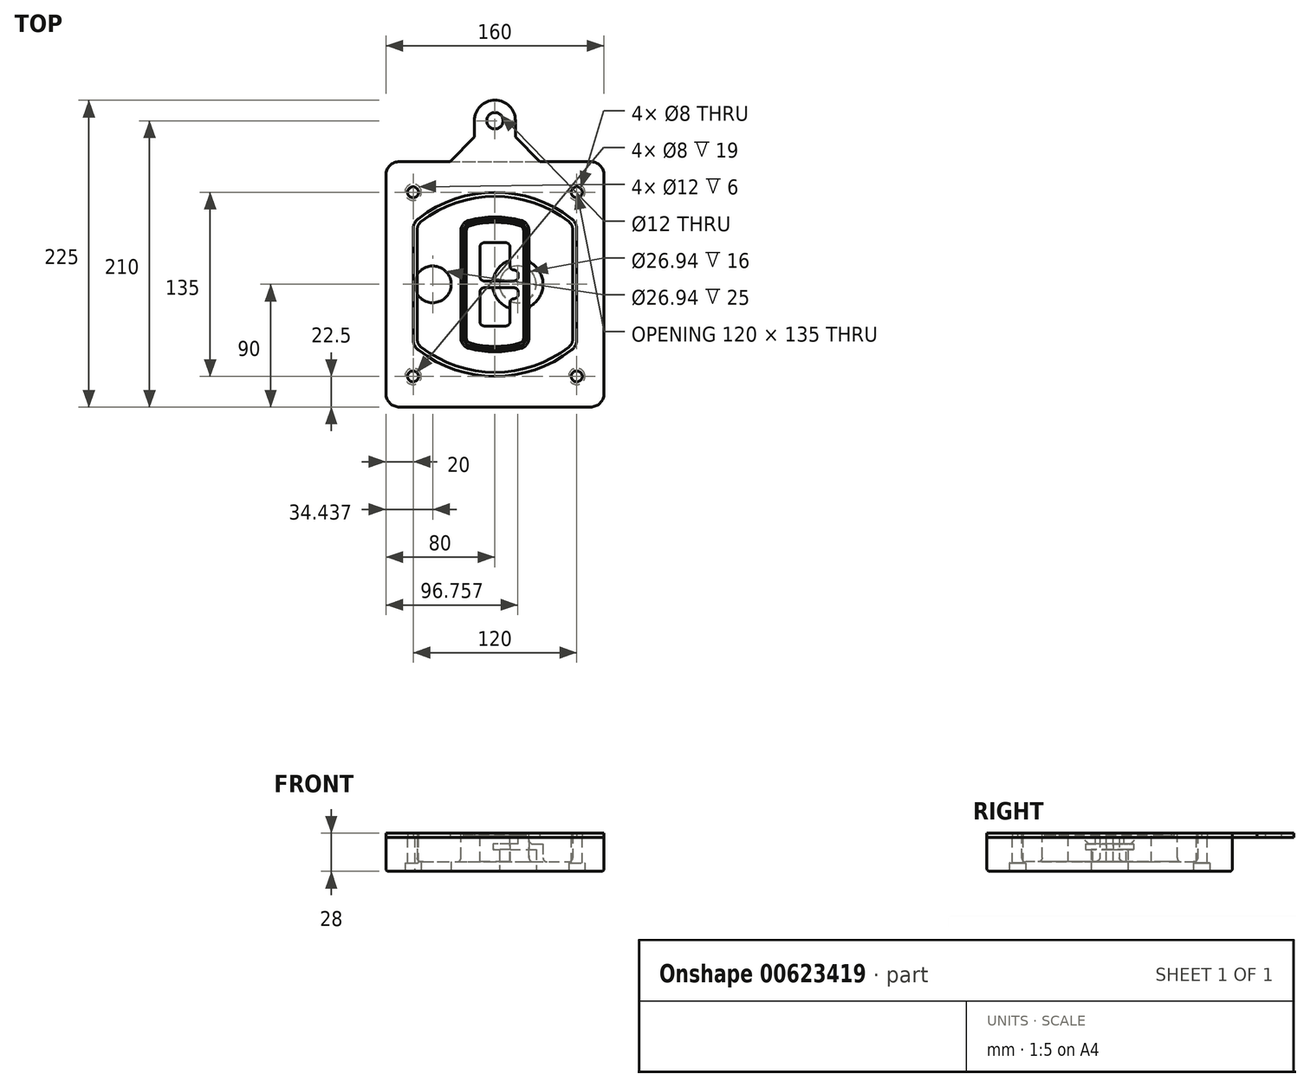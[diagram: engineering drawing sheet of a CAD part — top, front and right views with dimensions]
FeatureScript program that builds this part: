
annotation { "Feature Type Name" : "Feature", "Feature Type Description" : "" }
export const myFeature = defineFeature(function(context is Context, id is Id, definition is map)
    precondition{}
    {
        {
            var Q0;
            Q0=qCreatedBy(makeId("Top.planeOp"),FACE);
            var sketch = newSketch(context, id + "F0", { "sketchPlane" : qUnion([Q0])});
            skPoint(sketch, "E0.rect.middle", {"position": v(0, 0) * mm});
            skLineSegment(sketch, "E1.bottom", {"start": v(-70, -90) * mm, "end": v(70, -90) * mm});
            skLineSegment(sketch, "E1.top", {"start": v(-70, 90) * mm, "end": v(70, 90) * mm});
            skLineSegment(sketch, "E1.left", {"start": v(-80, -80) * mm, "end": v(-80, 80) * mm});
            skLineSegment(sketch, "E1.right", {"start": v(80, -80) * mm, "end": v(80, 80) * mm});
            skLineSegment(sketch, "E2", {"start": v(-80, 90) * mm, "end": v(80, -90) * mm, "construction": true});
            skLineSegment(sketch, "E3", {"start": v(80, 90) * mm, "end": v(-80, -90) * mm, "construction": true});
            skCircle(sketch, "E4", {"center": v(-60, 67.5) * mm, "radius": 4 * mm});
            skCircle(sketch, "E5", {"center": v(60, 67.5) * mm, "radius": 4 * mm});
            skCircle(sketch, "E6", {"center": v(60, -67.5) * mm, "radius": 4 * mm});
            skCircle(sketch, "E7", {"center": v(-60, -67.5) * mm, "radius": 4 * mm});
            skLineSegment(sketch, "E8", {"start": v(-60, 67.5) * mm, "end": v(60, 67.5) * mm, "construction": true});
            skLineSegment(sketch, "E9", {"start": v(60, 67.5) * mm, "end": v(60, -67.5) * mm, "construction": true});
            skLineSegment(sketch, "E10", {"start": v(60, -67.5) * mm, "end": v(-60, -67.5) * mm, "construction": true});
            skLineSegment(sketch, "E11", {"start": v(-60, -67.5) * mm, "end": v(-60, 67.5) * mm, "construction": true});
            skLineSegment(sketch, "E12", {"start": v(-60, 40.3) * mm, "end": v(-60, -40.3) * mm});
            skLineSegment(sketch, "E13", {"start": v(60, 40.3) * mm, "end": v(60, -40.3) * mm});
            skArc(sketch, "E14", {"start": v(56.15, 48.18) * mm, "mid": v(0, 67.5) * mm, "end": v(-56.15, 48.18) * mm});
            skArc(sketch, "E15", {"start": v(-56.15, -48.18) * mm, "mid": v(0, -67.5) * mm, "end": v(56.15, -48.18) * mm});
            skLineSegment(sketch, "E16", {"start": v(-60, 0) * mm, "end": v(60, 0) * mm, "construction": true});
            skPoint(sketch, "E17.visualSharp", {"position": v(-60, -45) * mm});
            skArc(sketch, "E17.filletArc", {"start": v(-60, -40.3) * mm, "mid": v(-58.99, -44.68) * mm, "end": v(-56.15, -48.18) * mm});
            skPoint(sketch, "E18.visualSharp", {"position": v(-60, 45) * mm});
            skArc(sketch, "E18.filletArc", {"start": v(-56.15, 48.18) * mm, "mid": v(-58.99, 44.68) * mm, "end": v(-60, 40.3) * mm});
            skPoint(sketch, "E19.visualSharp", {"position": v(60, 45) * mm});
            skArc(sketch, "E19.filletArc", {"start": v(60, 40.3) * mm, "mid": v(58.99, 44.68) * mm, "end": v(56.15, 48.18) * mm});
            skPoint(sketch, "E20.visualSharp", {"position": v(60, -45) * mm});
            skArc(sketch, "E20.filletArc", {"start": v(56.15, -48.18) * mm, "mid": v(58.99, -44.68) * mm, "end": v(60, -40.3) * mm});
            skPoint(sketch, "E21.visualSharp", {"position": v(-80, 90) * mm});
            skArc(sketch, "E21.filletArc", {"start": v(-70, 90) * mm, "mid": v(-77.07, 87.07) * mm, "end": v(-80, 80) * mm});
            skPoint(sketch, "E22.visualSharp", {"position": v(80, 90) * mm});
            skArc(sketch, "E22.filletArc", {"start": v(80, 80) * mm, "mid": v(77.07, 87.07) * mm, "end": v(70, 90) * mm});
            skPoint(sketch, "E23.visualSharp", {"position": v(80, -90) * mm});
            skArc(sketch, "E23.filletArc", {"start": v(70, -90) * mm, "mid": v(77.07, -87.07) * mm, "end": v(80, -80) * mm});
            skPoint(sketch, "E24.visualSharp", {"position": v(-80, -90) * mm});
            skArc(sketch, "E24.filletArc", {"start": v(-80, -80) * mm, "mid": v(-77.07, -87.07) * mm, "end": v(-70, -90) * mm});
            skArc(sketch, "E25.0", {"start": v(57, 40.3) * mm, "mid": v(56.3, 43.36) * mm, "end": v(54.3, 45.81) * mm});
            skLineSegment(sketch, "E25.1", {"start": v(57, 40.3) * mm, "end": v(57, -40.3) * mm});
            skArc(sketch, "E25.2", {"start": v(54.3, -45.81) * mm, "mid": v(56.3, -43.36) * mm, "end": v(57, -40.3) * mm});
            skArc(sketch, "E25.3", {"start": v(-54.3, -45.81) * mm, "mid": v(0, -64.5) * mm, "end": v(54.3, -45.81) * mm});
            skArc(sketch, "E25.4", {"start": v(-57, -40.3) * mm, "mid": v(-56.3, -43.36) * mm, "end": v(-54.3, -45.81) * mm});
            skArc(sketch, "E25.5", {"start": v(54.3, 45.81) * mm, "mid": v(0, 64.5) * mm, "end": v(-54.3, 45.81) * mm});
            skLineSegment(sketch, "E25.6", {"start": v(-57, 40.3) * mm, "end": v(-57, -40.3) * mm});
            skArc(sketch, "E25.7", {"start": v(-54.3, 45.81) * mm, "mid": v(-56.3, 43.36) * mm, "end": v(-57, 40.3) * mm});
            skArc(sketch, "E26.0", {"start": v(-58.62, 51.33) * mm, "mid": v(-62.58, 46.43) * mm, "end": v(-64, 40.3) * mm});
            skArc(sketch, "E26.1", {"start": v(58.62, 51.33) * mm, "mid": v(0, 71.5) * mm, "end": v(-58.62, 51.33) * mm});
            skArc(sketch, "E26.2", {"start": v(64, 40.3) * mm, "mid": v(62.58, 46.43) * mm, "end": v(58.62, 51.33) * mm});
            skLineSegment(sketch, "E26.3", {"start": v(64, 40.3) * mm, "end": v(64, -40.3) * mm});
            skArc(sketch, "E26.4", {"start": v(58.62, -51.33) * mm, "mid": v(62.58, -46.43) * mm, "end": v(64, -40.3) * mm});
            skLineSegment(sketch, "E26.5", {"start": v(-64, 40.3) * mm, "end": v(-64, -40.3) * mm});
            skArc(sketch, "E26.6", {"start": v(-58.62, -51.33) * mm, "mid": v(0, -71.5) * mm, "end": v(58.62, -51.33) * mm});
            skArc(sketch, "E26.7", {"start": v(-64, -40.3) * mm, "mid": v(-62.58, -46.43) * mm, "end": v(-58.62, -51.33) * mm});
            skSolve(sketch);
        }
        {
            var Q0;
            Q0=makeQuery(id+"F0.imprint","IMPRINT",FACE,{"disambiguationData":[TD([[makeQuery(id+"F0.imprint","IMPRINT",EDGE,{"derivedFrom":sQuery(id+"F0.wireOp",EDGE,"E1.bottom")}),1.0]])]});
            var Q1;
            Q1=makeQuery(id+"F0.imprint","IMPRINT",FACE,{"disambiguationData":[TD([[makeQuery(id+"F0.imprint","IMPRINT",EDGE,{"derivedFrom":sQuery(id+"F0.wireOp",EDGE,"E12")}),1.0]])]});
            var Q2;
            Q2=makeQuery(id+"F0.imprint","IMPRINT",FACE,{"disambiguationData":[TD([[makeQuery(id+"F0.imprint","IMPRINT",EDGE,{"derivedFrom":sQuery(id+"F0.wireOp",EDGE,"E25.0")}),1.0]])]});
            var Q3;
            Q3=makeQuery(id+"F0.imprint","IMPRINT",FACE,{"disambiguationData":[TD([[makeQuery(id+"F0.imprint","IMPRINT",EDGE,{"derivedFrom":sQuery(id+"F0.wireOp",EDGE,"E12")}),-1.0]])]});
            extrude(context, id + "F1", {"entities" : qUnion([Q0, Q1, Q2, Q3]), "oppositeDirection" : true, "depth" : 25 * mm});
        }
        {
            var Q0;
            Q0=makeQuery(id+"F0.imprint","IMPRINT",FACE,{"disambiguationData":[TD([[makeQuery(id+"F0.imprint","IMPRINT",EDGE,{"derivedFrom":sQuery(id+"F0.wireOp",EDGE,"E12")}),1.0]])]});
            extrude(context, id + "F2", {"entities" : qUnion([Q0]), "operationType" : NewBodyOperationType.ADD, "depth" : 3 * mm});
        }
        {
            var Q0;
            Q0=makeQuery(id+"F0.imprint","IMPRINT",FACE,{"disambiguationData":[TD([[makeQuery(id+"F0.imprint","IMPRINT",EDGE,{"derivedFrom":sQuery(id+"F0.wireOp",EDGE,"E25.0")}),1.0]])]});
            extrude(context, id + "F3", {"entities" : qUnion([Q0]), "operationType" : NewBodyOperationType.REMOVE, "oppositeDirection" : true, "depth" : 18 * mm});
        }
        {
            var Q0;
            Q0=makeQuery(id+"F2.opExtrude","CAP_FACE",FACE,{"disambiguationData":[OSD([sQuery(id+"F0.wireOp",EDGE,"E12"),sQuery(id+"F0.wireOp",EDGE,"E13"),sQuery(id+"F0.wireOp",EDGE,"E14"),sQuery(id+"F0.wireOp",EDGE,"E15"),sQuery(id+"F0.wireOp",EDGE,"E17.filletArc"),sQuery(id+"F0.wireOp",EDGE,"E18.filletArc"),sQuery(id+"F0.wireOp",EDGE,"E19.filletArc"),sQuery(id+"F0.wireOp",EDGE,"E20.filletArc"),sQuery(id+"F0.wireOp",EDGE,"E25.0"),sQuery(id+"F0.wireOp",EDGE,"E25.1"),sQuery(id+"F0.wireOp",EDGE,"E25.2"),sQuery(id+"F0.wireOp",EDGE,"E25.3"),sQuery(id+"F0.wireOp",EDGE,"E25.4"),sQuery(id+"F0.wireOp",EDGE,"E25.5"),sQuery(id+"F0.wireOp",EDGE,"E25.6"),sQuery(id+"F0.wireOp",EDGE,"E25.7")])],"isStart":false});
            var sketch = newSketch(context, id + "F4", { "sketchPlane" : qUnion([Q0])});
            skArc(sketch, "E27.0", {"start": v(-19.08, -46.97) * mm, "mid": v(0, -49.5) * mm, "end": v(19.08, -46.97) * mm});
            skArc(sketch, "E28.0", {"start": v(19.08, 46.97) * mm, "mid": v(0, 49.5) * mm, "end": v(-19.08, 46.97) * mm});
            skLineSegment(sketch, "E29", {"start": v(-25, 39.25) * mm, "end": v(-25, -39.25) * mm});
            skLineSegment(sketch, "E30", {"start": v(25, 39.25) * mm, "end": v(25, -39.25) * mm});
            skLineSegment(sketch, "E31", {"start": v(-25, 45.1) * mm, "end": v(25, 45.1) * mm, "construction": true});
            skLineSegment(sketch, "E32", {"start": v(-25, -45.1) * mm, "end": v(25, -45.1) * mm, "construction": true});
            skPoint(sketch, "E33.visualSharp", {"position": v(-25, 45.1) * mm});
            skArc(sketch, "E33.filletArc", {"start": v(-19.08, 46.97) * mm, "mid": v(-23.35, 44.11) * mm, "end": v(-25, 39.25) * mm});
            skPoint(sketch, "E34.visualSharp", {"position": v(25, 45.1) * mm});
            skArc(sketch, "E34.filletArc", {"start": v(25, 39.25) * mm, "mid": v(23.35, 44.11) * mm, "end": v(19.08, 46.97) * mm});
            skPoint(sketch, "E35.visualSharp", {"position": v(25, -45.1) * mm});
            skArc(sketch, "E35.filletArc", {"start": v(19.08, -46.97) * mm, "mid": v(23.35, -44.11) * mm, "end": v(25, -39.25) * mm});
            skPoint(sketch, "E36.visualSharp", {"position": v(-25, -45.1) * mm});
            skArc(sketch, "E36.filletArc", {"start": v(-25, -39.25) * mm, "mid": v(-23.35, -44.11) * mm, "end": v(-19.08, -46.97) * mm});
            skArc(sketch, "E37.0", {"start": v(54.3, 45.81) * mm, "mid": v(0, 64.5) * mm, "end": v(-54.3, 45.81) * mm});
            skArc(sketch, "E37.1", {"start": v(-54.3, 45.81) * mm, "mid": v(-56.3, 43.36) * mm, "end": v(-57, 40.3) * mm});
            skLineSegment(sketch, "E37.2", {"start": v(-57, 40.3) * mm, "end": v(-57, -40.3) * mm});
            skArc(sketch, "E37.3", {"start": v(-57, -40.3) * mm, "mid": v(-56.3, -43.36) * mm, "end": v(-54.3, -45.81) * mm});
            skArc(sketch, "E37.4", {"start": v(-54.3, -45.81) * mm, "mid": v(0, -64.5) * mm, "end": v(54.3, -45.81) * mm});
            skArc(sketch, "E37.5", {"start": v(54.3, -45.81) * mm, "mid": v(56.3, -43.36) * mm, "end": v(57, -40.3) * mm});
            skLineSegment(sketch, "E37.6", {"start": v(57, 40.3) * mm, "end": v(57, -40.3) * mm});
            skArc(sketch, "E37.7", {"start": v(57, 40.3) * mm, "mid": v(56.3, 43.36) * mm, "end": v(54.3, 45.81) * mm});
            skLineSegment(sketch, "E38.0", {"start": v(23, 39.25) * mm, "end": v(23, -39.25) * mm});
            skArc(sketch, "E38.1", {"start": v(18.56, -45.04) * mm, "mid": v(21.76, -42.9) * mm, "end": v(23, -39.25) * mm});
            skArc(sketch, "E38.2", {"start": v(-18.56, -45.04) * mm, "mid": v(0, -47.5) * mm, "end": v(18.56, -45.04) * mm});
            skArc(sketch, "E38.3", {"start": v(-23, -39.25) * mm, "mid": v(-21.76, -42.9) * mm, "end": v(-18.56, -45.04) * mm});
            skLineSegment(sketch, "E38.4", {"start": v(-23, 39.25) * mm, "end": v(-23, -39.25) * mm});
            skArc(sketch, "E38.5", {"start": v(23, 39.25) * mm, "mid": v(21.76, 42.9) * mm, "end": v(18.56, 45.04) * mm});
            skArc(sketch, "E38.6", {"start": v(-18.56, 45.04) * mm, "mid": v(-21.76, 42.9) * mm, "end": v(-23, 39.25) * mm});
            skArc(sketch, "E38.7", {"start": v(18.56, 45.04) * mm, "mid": v(0, 47.5) * mm, "end": v(-18.56, 45.04) * mm});
            skArc(sketch, "E39.0", {"start": v(21, 39.25) * mm, "mid": v(20.18, 41.68) * mm, "end": v(18.04, 43.1) * mm});
            skLineSegment(sketch, "E39.1", {"start": v(21, 39.25) * mm, "end": v(21, -39.25) * mm});
            skArc(sketch, "E39.2", {"start": v(18.04, -43.1) * mm, "mid": v(20.18, -41.68) * mm, "end": v(21, -39.25) * mm});
            skArc(sketch, "E39.3", {"start": v(-18.04, -43.1) * mm, "mid": v(0, -45.5) * mm, "end": v(18.04, -43.1) * mm});
            skArc(sketch, "E39.4", {"start": v(-21, -39.25) * mm, "mid": v(-20.18, -41.68) * mm, "end": v(-18.04, -43.1) * mm});
            skArc(sketch, "E39.5", {"start": v(18.04, 43.1) * mm, "mid": v(0, 45.5) * mm, "end": v(-18.04, 43.1) * mm});
            skLineSegment(sketch, "E39.6", {"start": v(-21, 39.25) * mm, "end": v(-21, -39.25) * mm});
            skArc(sketch, "E39.7", {"start": v(-18.04, 43.1) * mm, "mid": v(-20.18, 41.68) * mm, "end": v(-21, 39.25) * mm});
            skLineSegment(sketch, "E40", {"start": v(-25, 0) * mm, "end": v(25, 0) * mm, "construction": true});
            skLineSegment(sketch, "E41", {"start": v(-11, 5.5) * mm, "end": v(-11, 27.5) * mm});
            skLineSegment(sketch, "E42", {"start": v(-8, 30.5) * mm, "end": v(8, 30.5) * mm});
            skLineSegment(sketch, "E43", {"start": v(11, 27.5) * mm, "end": v(11, 13.5) * mm});
            skLineSegment(sketch, "E44", {"start": v(14, 10.5) * mm, "end": v(14, 10.5) * mm});
            skLineSegment(sketch, "E45", {"start": v(17, 7.5) * mm, "end": v(17, 5.5) * mm});
            skLineSegment(sketch, "E46", {"start": v(14, 2.5) * mm, "end": v(-8, 2.5) * mm});
            skPoint(sketch, "E47.visualSharp", {"position": v(-11, 30.5) * mm});
            skArc(sketch, "E47.filletArc", {"start": v(-8, 30.5) * mm, "mid": v(-10.12, 29.62) * mm, "end": v(-11, 27.5) * mm});
            skPoint(sketch, "E48.visualSharp", {"position": v(11, 30.5) * mm});
            skArc(sketch, "E48.filletArc", {"start": v(11, 27.5) * mm, "mid": v(10.12, 29.62) * mm, "end": v(8, 30.5) * mm});
            skPoint(sketch, "E49.visualSharp", {"position": v(11, 10.5) * mm});
            skArc(sketch, "E49.filletArc", {"start": v(11, 13.5) * mm, "mid": v(11.88, 11.38) * mm, "end": v(14, 10.5) * mm});
            skPoint(sketch, "E50.visualSharp", {"position": v(17, 10.5) * mm});
            skArc(sketch, "E50.filletArc", {"start": v(17, 7.5) * mm, "mid": v(16.12, 9.62) * mm, "end": v(14, 10.5) * mm});
            skPoint(sketch, "E51.visualSharp", {"position": v(17, 2.5) * mm});
            skArc(sketch, "E51.filletArc", {"start": v(14, 2.5) * mm, "mid": v(16.12, 3.38) * mm, "end": v(17, 5.5) * mm});
            skPoint(sketch, "E52.visualSharp", {"position": v(-11, 2.5) * mm});
            skArc(sketch, "E52.filletArc", {"start": v(-11, 5.5) * mm, "mid": v(-10.12, 3.38) * mm, "end": v(-8, 2.5) * mm});
            skLineSegment(sketch, "E53.0.MirrorCS", {"start": v(14, -2.5) * mm, "end": v(-8, -2.5) * mm});
            skArc(sketch, "E54.0.MirrorCS", {"start": v(-11, -5.5) * mm, "mid": v(-10.12, -3.38) * mm, "end": v(-8, -2.5) * mm});
            skLineSegment(sketch, "E55.0.MirrorCS", {"start": v(-11, -5.5) * mm, "end": v(-11, -27.5) * mm});
            skArc(sketch, "E56.0.MirrorCS", {"start": v(-8, -30.5) * mm, "mid": v(-10.12, -29.62) * mm, "end": v(-11, -27.5) * mm});
            skLineSegment(sketch, "E57.0.MirrorCS", {"start": v(-8, -30.5) * mm, "end": v(8, -30.5) * mm});
            skArc(sketch, "E58.0.MirrorCS", {"start": v(11, -27.5) * mm, "mid": v(10.12, -29.62) * mm, "end": v(8, -30.5) * mm});
            skLineSegment(sketch, "E59.0.MirrorCS", {"start": v(11, -27.5) * mm, "end": v(11, -13.5) * mm});
            skArc(sketch, "E60.0.MirrorCS", {"start": v(11, -13.5) * mm, "mid": v(11.88, -11.38) * mm, "end": v(14, -10.5) * mm});
            skArc(sketch, "E61.0.MirrorCS", {"start": v(17, -7.5) * mm, "mid": v(16.12, -9.62) * mm, "end": v(14, -10.5) * mm});
            skLineSegment(sketch, "E62.0.MirrorCS", {"start": v(17, -7.5) * mm, "end": v(17, -5.5) * mm});
            skArc(sketch, "E63.0.MirrorCS", {"start": v(14, -2.5) * mm, "mid": v(16.12, -3.38) * mm, "end": v(17, -5.5) * mm});
            skSolve(sketch);
        }
        {
            var Q0;
            Q0=makeQuery(id+"F4.imprint","IMPRINT",FACE,{"disambiguationData":[TD([[makeQuery(id+"F4.imprint","IMPRINT",EDGE,{"derivedFrom":sQuery(id+"F4.wireOp",EDGE,"E27.0")}),1.0]])]});
            var Q1;
            Q1=makeQuery(id+"F4.imprint","IMPRINT",FACE,{"disambiguationData":[TD([[makeQuery(id+"F4.imprint","IMPRINT",EDGE,{"derivedFrom":sQuery(id+"F4.wireOp",EDGE,"E38.0")}),-1.0]])]});
            var Q2;
            Q2=makeQuery(id+"F4.imprint","IMPRINT",FACE,{"disambiguationData":[TD([[makeQuery(id+"F4.imprint","IMPRINT",EDGE,{"derivedFrom":sQuery(id+"F4.wireOp",EDGE,"E39.0")}),1.0]])]});
            extrude(context, id + "F5", {"entities" : qUnion([Q0, Q1, Q2]), "operationType" : NewBodyOperationType.ADD, "endBound" : BoundingType.UP_TO_NEXT, "oppositeDirection" : true, "depth" : 25 * mm});
        }
        {
            var Q0;
            Q0=makeQuery(id+"F4.imprint","IMPRINT",FACE,{"disambiguationData":[TD([[makeQuery(id+"F4.imprint","IMPRINT",EDGE,{"derivedFrom":sQuery(id+"F4.wireOp",EDGE,"E38.0")}),-1.0]])]});
            extrude(context, id + "F6", {"entities" : qUnion([Q0]), "operationType" : NewBodyOperationType.REMOVE, "oppositeDirection" : true, "depth" : 2 * mm});
        }
        {
            var Q0;
            Q0=makeQuery(id+"F1.opExtrude","CAP_FACE",FACE,{"disambiguationData":[OSD([sQuery(id+"F0.wireOp",EDGE,"E1.bottom"),sQuery(id+"F0.wireOp",EDGE,"E1.top"),sQuery(id+"F0.wireOp",EDGE,"E1.left"),sQuery(id+"F0.wireOp",EDGE,"E1.right"),sQuery(id+"F0.wireOp",EDGE,"E4"),sQuery(id+"F0.wireOp",EDGE,"E5"),sQuery(id+"F0.wireOp",EDGE,"E6"),sQuery(id+"F0.wireOp",EDGE,"E7"),sQuery(id+"F0.wireOp",EDGE,"E21.filletArc"),sQuery(id+"F0.wireOp",EDGE,"E22.filletArc"),sQuery(id+"F0.wireOp",EDGE,"E23.filletArc"),sQuery(id+"F0.wireOp",EDGE,"E24.filletArc")])],"isStart":false});
            var sketch = newSketch(context, id + "F7", { "sketchPlane" : qUnion([Q0])});
            skCircle(sketch, "E64", {"center": v(16.76, 0) * mm, "radius": 13.47 * mm});
            skCircle(sketch, "E65", {"center": v(-45.56, 0) * mm, "radius": 13.47 * mm});
            skLineSegment(sketch, "E66", {"start": v(80, 0) * mm, "end": v(-80, 0) * mm});
            skCircle(sketch, "E67", {"center": v(16.76, 0) * mm, "radius": 18.47 * mm});
            skCircle(sketch, "E68", {"center": v(60, -67.5) * mm, "radius": 6 * mm});
            skCircle(sketch, "E69", {"center": v(-60, -67.5) * mm, "radius": 6 * mm});
            skCircle(sketch, "E70", {"center": v(-60, 67.5) * mm, "radius": 6 * mm});
            skCircle(sketch, "E71", {"center": v(60, 67.5) * mm, "radius": 6 * mm});
            skSolve(sketch);
        }
        {
            var Q0;
            {var subQ1=sQuery(id+"F7.wireOp",EDGE,"E66");var subQ4=sQuery(id+"F7.wireOp",EDGE,"E64");var subQ6=makeQuery(id+"F7.imprint","INTERSECT",VERTEX,{"disambiguationData":[OD(0.0)],"derivedFrom":[subQ4,subQ1]});Q0=makeQuery(id+"F7.imprint","IMPRINT",FACE,{"disambiguationData":[TD([[makeQuery(id+"F7.imprint","IMPRINT",EDGE,{"disambiguationData":[TD([[subQ6,-1.0]])],"derivedFrom":subQ4}),-1.0]])]});}
            var Q1;
            {var subQ0=sQuery(id+"F7.wireOp",EDGE,"E66");var subQ1=sQuery(id+"F7.wireOp",EDGE,"E64");var subQ3=makeQuery(id+"F7.imprint","INTERSECT",VERTEX,{"disambiguationData":[OD(0.0)],"derivedFrom":[subQ1,subQ0]});Q1=makeQuery(id+"F7.imprint","IMPRINT",FACE,{"disambiguationData":[TD([[makeQuery(id+"F7.imprint","IMPRINT",EDGE,{"disambiguationData":[TD([[subQ3,-1.0]])],"derivedFrom":subQ1}),1.0]])]});}
            var Q2;
            {var subQ0=sQuery(id+"F7.wireOp",EDGE,"E66");var subQ1=sQuery(id+"F7.wireOp",EDGE,"E64");var subQ3=makeQuery(id+"F7.imprint","INTERSECT",VERTEX,{"disambiguationData":[OD(0.0)],"derivedFrom":[subQ1,subQ0]});Q2=makeQuery(id+"F7.imprint","IMPRINT",FACE,{"disambiguationData":[TD([[makeQuery(id+"F7.imprint","IMPRINT",EDGE,{"disambiguationData":[TD([[subQ3,1.0]])],"derivedFrom":subQ1}),1.0]])]});}
            var Q3;
            {var subQ1=sQuery(id+"F7.wireOp",EDGE,"E66");var subQ4=sQuery(id+"F7.wireOp",EDGE,"E64");var subQ6=makeQuery(id+"F7.imprint","INTERSECT",VERTEX,{"disambiguationData":[OD(0.0)],"derivedFrom":[subQ4,subQ1]});Q3=makeQuery(id+"F7.imprint","IMPRINT",FACE,{"disambiguationData":[TD([[makeQuery(id+"F7.imprint","IMPRINT",EDGE,{"disambiguationData":[TD([[subQ6,1.0]])],"derivedFrom":subQ4}),-1.0]])]});}
            extrude(context, id + "F8", {"entities" : qUnion([Q0, Q1, Q2, Q3]), "operationType" : NewBodyOperationType.ADD, "oppositeDirection" : true, "depth" : 20 * mm});
        }
        {
            var Q0;
            {var subQ0=sQuery(id+"F7.wireOp",EDGE,"E66");var subQ1=sQuery(id+"F7.wireOp",EDGE,"E64");var subQ3=makeQuery(id+"F7.imprint","INTERSECT",VERTEX,{"disambiguationData":[OD(0.0)],"derivedFrom":[subQ1,subQ0]});Q0=makeQuery(id+"F7.imprint","IMPRINT",FACE,{"disambiguationData":[TD([[makeQuery(id+"F7.imprint","IMPRINT",EDGE,{"disambiguationData":[TD([[subQ3,-1.0]])],"derivedFrom":subQ1}),1.0]])]});}
            var Q1;
            {var subQ0=sQuery(id+"F7.wireOp",EDGE,"E66");var subQ1=sQuery(id+"F7.wireOp",EDGE,"E64");var subQ3=makeQuery(id+"F7.imprint","INTERSECT",VERTEX,{"disambiguationData":[OD(0.0)],"derivedFrom":[subQ1,subQ0]});Q1=makeQuery(id+"F7.imprint","IMPRINT",FACE,{"disambiguationData":[TD([[makeQuery(id+"F7.imprint","IMPRINT",EDGE,{"disambiguationData":[TD([[subQ3,1.0]])],"derivedFrom":subQ1}),1.0]])]});}
            extrude(context, id + "F9", {"entities" : qUnion([Q0, Q1]), "operationType" : NewBodyOperationType.REMOVE, "oppositeDirection" : true, "depth" : 16 * mm});
        }
        {
            var Q0;
            {var subQ0=sQuery(id+"F7.wireOp",EDGE,"E66");var subQ1=sQuery(id+"F7.wireOp",EDGE,"E65");var subQ3=makeQuery(id+"F7.imprint","INTERSECT",VERTEX,{"disambiguationData":[OD(0.0)],"derivedFrom":[subQ1,subQ0]});Q0=makeQuery(id+"F7.imprint","IMPRINT",FACE,{"disambiguationData":[TD([[makeQuery(id+"F7.imprint","IMPRINT",EDGE,{"disambiguationData":[TD([[subQ3,-1.0]])],"derivedFrom":subQ1}),1.0]])]});}
            var Q1;
            {var subQ0=sQuery(id+"F7.wireOp",EDGE,"E66");var subQ1=sQuery(id+"F7.wireOp",EDGE,"E65");var subQ3=makeQuery(id+"F7.imprint","INTERSECT",VERTEX,{"disambiguationData":[OD(0.0)],"derivedFrom":[subQ1,subQ0]});Q1=makeQuery(id+"F7.imprint","IMPRINT",FACE,{"disambiguationData":[TD([[makeQuery(id+"F7.imprint","IMPRINT",EDGE,{"disambiguationData":[TD([[subQ3,1.0]])],"derivedFrom":subQ1}),1.0]])]});}
            extrude(context, id + "F10", {"entities" : qUnion([Q0, Q1]), "operationType" : NewBodyOperationType.REMOVE, "oppositeDirection" : true, "depth" : 25 * mm});
        }
        {
            var Q0;
            Q0=makeQuery(id+"F7.imprint","IMPRINT",FACE,{"disambiguationData":[TD([[makeQuery(id+"F7.imprint","IMPRINT",EDGE,{"derivedFrom":sQuery(id+"F7.wireOp",EDGE,"E68")}),1.0]])]});
            var Q1;
            Q1=makeQuery(id+"F7.imprint","IMPRINT",FACE,{"disambiguationData":[TD([[makeQuery(id+"F7.imprint","IMPRINT",EDGE,{"derivedFrom":makeQuery(id+"F1.opExtrude","CAP_EDGE",EDGE,{"disambiguationData":[OSD([sQuery(id+"F0.wireOp",EDGE,"E5")])],"isStart":false})}),-1.0]])]});
            var Q2;
            Q2=makeQuery(id+"F7.imprint","IMPRINT",FACE,{"disambiguationData":[TD([[makeQuery(id+"F7.imprint","IMPRINT",EDGE,{"derivedFrom":sQuery(id+"F7.wireOp",EDGE,"E69")}),1.0]])]});
            var Q3;
            Q3=makeQuery(id+"F7.imprint","IMPRINT",FACE,{"disambiguationData":[TD([[makeQuery(id+"F7.imprint","IMPRINT",EDGE,{"derivedFrom":makeQuery(id+"F1.opExtrude","CAP_EDGE",EDGE,{"disambiguationData":[OSD([sQuery(id+"F0.wireOp",EDGE,"E4")])],"isStart":false})}),-1.0]])]});
            var Q4;
            Q4=makeQuery(id+"F7.imprint","IMPRINT",FACE,{"disambiguationData":[TD([[makeQuery(id+"F7.imprint","IMPRINT",EDGE,{"derivedFrom":sQuery(id+"F7.wireOp",EDGE,"E70")}),1.0]])]});
            var Q5;
            Q5=makeQuery(id+"F7.imprint","IMPRINT",FACE,{"disambiguationData":[TD([[makeQuery(id+"F7.imprint","IMPRINT",EDGE,{"derivedFrom":makeQuery(id+"F1.opExtrude","CAP_EDGE",EDGE,{"disambiguationData":[OSD([sQuery(id+"F0.wireOp",EDGE,"E7")])],"isStart":false})}),-1.0]])]});
            var Q6;
            Q6=makeQuery(id+"F7.imprint","IMPRINT",FACE,{"disambiguationData":[TD([[makeQuery(id+"F7.imprint","IMPRINT",EDGE,{"derivedFrom":sQuery(id+"F7.wireOp",EDGE,"E71")}),1.0]])]});
            var Q7;
            Q7=makeQuery(id+"F7.imprint","IMPRINT",FACE,{"disambiguationData":[TD([[makeQuery(id+"F7.imprint","IMPRINT",EDGE,{"derivedFrom":makeQuery(id+"F1.opExtrude","CAP_EDGE",EDGE,{"disambiguationData":[OSD([sQuery(id+"F0.wireOp",EDGE,"E6")])],"isStart":false})}),-1.0]])]});
            extrude(context, id + "F11", {"entities" : qUnion([Q0, Q1, Q2, Q3, Q4, Q5, Q6, Q7]), "operationType" : NewBodyOperationType.REMOVE, "oppositeDirection" : true, "depth" : 6 * mm});
        }
        {
            var Q0;
            Q0=makeQuery(id+"F9.boolean.opBoolean","COPY",FACE,{"derivedFrom":makeQuery(id+"F9.opExtrude","CAP_FACE",FACE,{"disambiguationData":[OSD([sQuery(id+"F7.wireOp",EDGE,"E64")])],"isStart":false})});
            var sketch = newSketch(context, id + "F12", { "sketchPlane" : qUnion([Q0])});
            skArc(sketch, "E72.0", {"start": v(11, 17.55) * mm, "mid": v(2.57, 11.82) * mm, "end": v(-1.54, 2.5) * mm});
            skArc(sketch, "E72.1", {"start": v(-1.54, -2.5) * mm, "mid": v(2.57, -11.82) * mm, "end": v(11, -17.55) * mm});
            skLineSegment(sketch, "E73", {"start": v(-1.54, -2.5) * mm, "end": v(14, -2.5) * mm});
            skLineSegment(sketch, "E74.0", {"start": v(14, 2.5) * mm, "end": v(-1.54, 2.5) * mm});
            skArc(sketch, "E74.1", {"start": v(14, 2.5) * mm, "mid": v(16.12, 3.38) * mm, "end": v(17, 5.5) * mm});
            skLineSegment(sketch, "E74.2", {"start": v(17, 7.5) * mm, "end": v(17, 5.5) * mm});
            skArc(sketch, "E74.3", {"start": v(17, 7.5) * mm, "mid": v(16.12, 9.62) * mm, "end": v(14, 10.5) * mm});
            skArc(sketch, "E74.4", {"start": v(11, 13.5) * mm, "mid": v(11.88, 11.38) * mm, "end": v(14, 10.5) * mm});
            skLineSegment(sketch, "E74.5", {"start": v(11, 17.55) * mm, "end": v(11, 13.5) * mm});
            skLineSegment(sketch, "E74.7", {"start": v(14, -2.5) * mm, "end": v(-1.54, -2.5) * mm});
            skArc(sketch, "E74.8", {"start": v(14, -2.5) * mm, "mid": v(16.12, -3.38) * mm, "end": v(17, -5.5) * mm});
            skLineSegment(sketch, "E74.9", {"start": v(17, -7.5) * mm, "end": v(17, -5.5) * mm});
            skArc(sketch, "E74.10", {"start": v(17, -7.5) * mm, "mid": v(16.12, -9.62) * mm, "end": v(14, -10.5) * mm});
            skArc(sketch, "E74.11", {"start": v(11, -13.5) * mm, "mid": v(11.88, -11.38) * mm, "end": v(14, -10.5) * mm});
            skLineSegment(sketch, "E74.12", {"start": v(11, -17.55) * mm, "end": v(11, -13.5) * mm});
            skPoint(sketch, "E75.orphan", {"position": v(11, -27.5) * mm});
            skPoint(sketch, "E76.orphan", {"position": v(-8, -2.5) * mm});
            skPoint(sketch, "E77.orphan", {"position": v(-8, 2.5) * mm});
            skPoint(sketch, "E78.orphan", {"position": v(11, 27.5) * mm});
            skSolve(sketch);
        }
        {
            var Q0;
            {var subQ7=sQuery(id+"F12.wireOp",EDGE,"E72.0");var subQ14=sQuery(id+"F12.wireOp",EDGE,"E72.1");var subQ16=sQuery(id+"F12.wireOp",EDGE,"E74.1");var subQ18=sQuery(id+"F12.wireOp",EDGE,"E74.8");Q0=qUnion([makeQuery(id+"F12.imprint","IMPRINT",FACE,{"disambiguationData":[TD([[makeQuery(id+"F12.imprint","IMPRINT",EDGE,{"derivedFrom":subQ7}),1.0]])]}),makeQuery(id+"F12.imprint","IMPRINT",FACE,{"disambiguationData":[TD([[makeQuery(id+"F12.imprint","IMPRINT",EDGE,{"derivedFrom":subQ14}),1.0]])]}),makeQuery(id+"F12.imprint","IMPRINT",FACE,{"disambiguationData":[TD([[makeQuery(id+"F12.imprint","IMPRINT",EDGE,{"derivedFrom":subQ16}),1.0]])]}),makeQuery(id+"F12.imprint","IMPRINT",FACE,{"disambiguationData":[TD([[makeQuery(id+"F12.imprint","IMPRINT",EDGE,{"derivedFrom":subQ18}),-1.0]])]})]);}
            var Q1;
            Q1=makeQuery(id+"F5.boolean.opBoolean","SPLIT",FACE,{"disambiguationData":[TD([makeQuery(id+"F5.opExtrude","SWEPT_FACE",FACE,{"disambiguationData":[OSD([sQuery(id+"F4.wireOp",EDGE,"E41")])]})])],"derivedFrom":makeQuery(id+"F3.boolean.opBoolean","COPY",FACE,{"derivedFrom":makeQuery(id+"F3.opExtrude","CAP_FACE",FACE,{"disambiguationData":[OSD([sQuery(id+"F0.wireOp",EDGE,"E25.0"),sQuery(id+"F0.wireOp",EDGE,"E25.1"),sQuery(id+"F0.wireOp",EDGE,"E25.2"),sQuery(id+"F0.wireOp",EDGE,"E25.3"),sQuery(id+"F0.wireOp",EDGE,"E25.4"),sQuery(id+"F0.wireOp",EDGE,"E25.5"),sQuery(id+"F0.wireOp",EDGE,"E25.6"),sQuery(id+"F0.wireOp",EDGE,"E25.7")])],"isStart":false})})});
            extrude(context, id + "F13", {"entities" : qUnion([Q0]), "operationType" : NewBodyOperationType.REMOVE, "endBound" : BoundingType.UP_TO_SURFACE, "endBoundEntityFace" : qUnion([Q1]), "depth" : 25 * mm});
        }
        {
            var Q0;
            Q0=makeQuery(id+"F3.boolean.opBoolean","COPY",EDGE,{"derivedFrom":makeQuery(id+"F3.opExtrude","CAP_EDGE",EDGE,{"disambiguationData":[OSD([sQuery(id+"F0.wireOp",EDGE,"E25.6")])],"isStart":false})});
            var Q1;
            Q1=makeQuery(id+"F8.boolean.opBoolean","INTERSECT",EDGE,{"derivedFrom":[makeQuery(id+"F5.opExtrude","SWEPT_FACE",FACE,{"disambiguationData":[OSD([sQuery(id+"F4.wireOp",EDGE,"E30")])]}),makeQuery(id+"F8.opExtrude","CAP_FACE",FACE,{"disambiguationData":[OSD([sQuery(id+"F7.wireOp",EDGE,"E67")])],"isStart":false})]});
            var Q2;
            Q2=makeQuery(id+"F8.boolean.opBoolean","INTERSECT",EDGE,{"disambiguationData":[OD(1.0)],"derivedFrom":[makeQuery(id+"F5.opExtrude","SWEPT_FACE",FACE,{"disambiguationData":[OSD([sQuery(id+"F4.wireOp",EDGE,"E30")])]}),makeQuery(id+"F8.opExtrude","SWEPT_FACE",FACE,{"disambiguationData":[OSD([sQuery(id+"F7.wireOp",EDGE,"E67")])]})]});
            var Q3;
            {var subQ0=sQuery(id+"F4.wireOp",EDGE,"E30");Q3=makeQuery(id+"F8.boolean.opBoolean","SPLIT",EDGE,{"disambiguationData":[TD([makeQuery(id+"F5.opExtrude","SWEPT_FACE",FACE,{"disambiguationData":[OSD([sQuery(id+"F4.wireOp",EDGE,"E35.filletArc")])]})])],"derivedFrom":makeQuery(id+"F5.opExtrude","CAP_EDGE",EDGE,{"disambiguationData":[OSD([subQ0])],"isStart":false})});}
            var Q4;
            {var subQ0=sQuery(id+"F0.wireOp",EDGE,"E25.7");var subQ1=sQuery(id+"F0.wireOp",EDGE,"E25.1");var subQ2=sQuery(id+"F0.wireOp",EDGE,"E25.6");var subQ3=sQuery(id+"F0.wireOp",EDGE,"E25.5");var subQ4=sQuery(id+"F0.wireOp",EDGE,"E25.4");var subQ5=sQuery(id+"F0.wireOp",EDGE,"E25.0");var subQ6=sQuery(id+"F0.wireOp",EDGE,"E25.2");var subQ7=sQuery(id+"F0.wireOp",EDGE,"E25.3");Q4=makeQuery(id+"F8.boolean.opBoolean","INTERSECT",EDGE,{"derivedFrom":[makeQuery(id+"F5.boolean.opBoolean","SPLIT",FACE,{"disambiguationData":[TD([makeQuery(id+"F2.opExtrude","SWEPT_FACE",FACE,{"disambiguationData":[OSD([subQ5])]})])],"derivedFrom":makeQuery(id+"F3.boolean.opBoolean","COPY",FACE,{"derivedFrom":makeQuery(id+"F3.opExtrude","CAP_FACE",FACE,{"disambiguationData":[OSD([subQ5,subQ1,subQ6,subQ7,subQ4,subQ3,subQ2,subQ0])],"isStart":false})})}),makeQuery(id+"F8.opExtrude","SWEPT_FACE",FACE,{"disambiguationData":[OSD([sQuery(id+"F7.wireOp",EDGE,"E67")])]})]});}
            var Q5;
            Q5=makeQuery(id+"F8.boolean.opBoolean","INTERSECT",EDGE,{"disambiguationData":[OD(0.0)],"derivedFrom":[makeQuery(id+"F5.opExtrude","SWEPT_FACE",FACE,{"disambiguationData":[OSD([sQuery(id+"F4.wireOp",EDGE,"E30")])]}),makeQuery(id+"F8.opExtrude","SWEPT_FACE",FACE,{"disambiguationData":[OSD([sQuery(id+"F7.wireOp",EDGE,"E67")])]})]});
            fillet(context, id + "F14", {"entities" : qUnion([Q0, Q1, Q2, Q3, Q4, Q5]), "radius" : 3 * mm, "tangentPropagation" : true, "allowEdgeOverflow" : false});
        }
        {
            var Q0;
            Q0=makeQuery(id+"F1.opExtrude","CAP_EDGE",EDGE,{"disambiguationData":[OSD([sQuery(id+"F0.wireOp",EDGE,"E1.bottom")])],"isStart":false});
            fillet(context, id + "F15", {"entities" : qUnion([Q0]), "radius" : 2 * mm, "tangentPropagation" : true, "allowEdgeOverflow" : false});
        }
        {
            var Q0;
            {var subQ0=sQuery(id+"F0.wireOp",EDGE,"E21.filletArc");var subQ1=sQuery(id+"F0.wireOp",EDGE,"E7");var subQ2=sQuery(id+"F0.wireOp",EDGE,"E6");var subQ3=sQuery(id+"F0.wireOp",EDGE,"E5");var subQ4=sQuery(id+"F0.wireOp",EDGE,"E4");var subQ5=sQuery(id+"F0.wireOp",EDGE,"E22.filletArc");var subQ6=sQuery(id+"F0.wireOp",EDGE,"E1.bottom");var subQ7=sQuery(id+"F0.wireOp",EDGE,"E1.right");var subQ8=sQuery(id+"F0.wireOp",EDGE,"E1.top");var subQ9=sQuery(id+"F0.wireOp",EDGE,"E1.left");var subQ10=sQuery(id+"F0.wireOp",EDGE,"E23.filletArc");var subQ11=sQuery(id+"F0.wireOp",EDGE,"E24.filletArc");Q0=makeQuery(id+"F2.boolean.opBoolean","SPLIT",FACE,{"disambiguationData":[TD([makeQuery(id+"F1.opExtrude","SWEPT_FACE",FACE,{"disambiguationData":[OSD([subQ6])]})])],"derivedFrom":makeQuery(id+"F1.opExtrude","CAP_FACE",FACE,{"disambiguationData":[OSD([subQ6,subQ8,subQ9,subQ7,subQ4,subQ3,subQ2,subQ1,subQ0,subQ5,subQ10,subQ11])],"isStart":true})});}
            var sketch = newSketch(context, id + "F16", { "sketchPlane" : qUnion([Q0])});
            skLineSegment(sketch, "E79.0", {"start": v(-70, 90) * mm, "end": v(70, 90) * mm});
            skArc(sketch, "E79.1", {"start": v(-70, 90) * mm, "mid": v(-77.07, 87.07) * mm, "end": v(-80, 80) * mm});
            skLineSegment(sketch, "E79.2", {"start": v(-80, -80) * mm, "end": v(-80, 80) * mm});
            skArc(sketch, "E79.3", {"start": v(-80, -80) * mm, "mid": v(-77.07, -87.07) * mm, "end": v(-70, -90) * mm});
            skLineSegment(sketch, "E79.4", {"start": v(-70, -90) * mm, "end": v(70, -90) * mm});
            skArc(sketch, "E79.5", {"start": v(70, -90) * mm, "mid": v(77.07, -87.07) * mm, "end": v(80, -80) * mm});
            skLineSegment(sketch, "E79.6", {"start": v(80, -80) * mm, "end": v(80, 80) * mm});
            skArc(sketch, "E79.7", {"start": v(80, 80) * mm, "mid": v(77.07, 87.07) * mm, "end": v(70, 90) * mm});
            skArc(sketch, "E79.8", {"start": v(56.15, 48.18) * mm, "mid": v(0, 67.5) * mm, "end": v(-56.15, 48.18) * mm});
            skLineSegment(sketch, "E79.9.0", {"start": v(60, -40.3) * mm, "end": v(60, 40.3) * mm});
            skArc(sketch, "E79.9.1", {"start": v(60, 40.3) * mm, "mid": v(58.99, 44.68) * mm, "end": v(56.15, 48.18) * mm});
            skArc(sketch, "E79.9.2", {"start": v(56.15, 48.18) * mm, "mid": v(0, 67.5) * mm, "end": v(-56.15, 48.18) * mm});
            skArc(sketch, "E79.9.3", {"start": v(-56.15, 48.18) * mm, "mid": v(-58.99, 44.68) * mm, "end": v(-60, 40.3) * mm});
            skLineSegment(sketch, "E79.9.4", {"start": v(-60, 40.3) * mm, "end": v(-60, -40.3) * mm});
            skArc(sketch, "E79.9.5", {"start": v(-60, -40.3) * mm, "mid": v(-58.99, -44.68) * mm, "end": v(-56.15, -48.18) * mm});
            skArc(sketch, "E79.9.6", {"start": v(-56.15, -48.18) * mm, "mid": v(0, -67.5) * mm, "end": v(56.15, -48.18) * mm});
            skArc(sketch, "E79.9.7", {"start": v(56.15, -48.18) * mm, "mid": v(58.99, -44.68) * mm, "end": v(60, -40.3) * mm});
            skLineSegment(sketch, "E80", {"start": v(0, 76.98) * mm, "end": v(0, 120) * mm, "construction": true});
            skPoint(sketch, "E80.startSnap0", {"position": v(0, 90) * mm});
            skCircle(sketch, "E81", {"center": v(0, 120) * mm, "radius": 6 * mm});
            skArc(sketch, "E82", {"start": v(15, 120) * mm, "mid": v(0, 135) * mm, "end": v(-15, 120) * mm});
            skLineSegment(sketch, "E83", {"start": v(-15, 120) * mm, "end": v(-15, 108) * mm});
            skLineSegment(sketch, "E84", {"start": v(-15, 108) * mm, "end": v(-33, 90) * mm});
            skLineSegment(sketch, "E85.MirrorCS", {"start": v(15, 120) * mm, "end": v(15, 108) * mm});
            skLineSegment(sketch, "E86.MirrorCS", {"start": v(15, 108) * mm, "end": v(33, 90) * mm});
            skLineSegment(sketch, "E87", {"start": v(-84.68, 0) * mm, "end": v(88.55, 0) * mm, "construction": true});
            skPoint(sketch, "E87.startSnap0", {"position": v(-80, 0) * mm});
            skPoint(sketch, "E87.endSnap0", {"position": v(80, 0) * mm});
            skArc(sketch, "E88.MirrorCS", {"start": v(15, -120) * mm, "mid": v(0, -135) * mm, "end": v(-15, -120) * mm});
            skPoint(sketch, "E89.MirrorP", {"position": v(0, -90) * mm});
            skCircle(sketch, "E90.MirrorC", {"center": v(0, -120) * mm, "radius": 6 * mm});
            skLineSegment(sketch, "E91.MirrorCS", {"start": v(15, -120) * mm, "end": v(15, -108) * mm});
            skLineSegment(sketch, "E92.MirrorCS", {"start": v(15, -108) * mm, "end": v(33, -90) * mm});
            skLineSegment(sketch, "E93.MirrorCS", {"start": v(-15, -108) * mm, "end": v(-33, -90) * mm});
            skLineSegment(sketch, "E94.MirrorCS", {"start": v(0, -76.98) * mm, "end": v(0, -120) * mm, "construction": true});
            skLineSegment(sketch, "E95.MirrorCS", {"start": v(-15, -120) * mm, "end": v(-15, -108) * mm});
            skSolve(sketch);
        }
        {
            var Q0;
            Q0=makeQuery(id+"F16.imprint","IMPRINT",FACE,{"disambiguationData":[TD([[makeQuery(id+"F16.imprint","IMPRINT",EDGE,{"derivedFrom":sQuery(id+"F16.wireOp",EDGE,"E81")}),-1.0]])]});
            var Q1;
            {var subQ1=sQuery(id+"F16.wireOp",EDGE,"E79.1");Q1=makeQuery(id+"F16.imprint","IMPRINT",FACE,{"disambiguationData":[TD([[makeQuery(id+"F16.imprint","IMPRINT",EDGE,{"derivedFrom":subQ1}),1.0]])]});}
            var Q2;
            Q2=makeQuery(id+"F16.imprint","IMPRINT",FACE,{"disambiguationData":[TD([[makeQuery(id+"F16.imprint","IMPRINT",EDGE,{"derivedFrom":sQuery(id+"F16.wireOp",EDGE,"E88.MirrorCS")}),-1.0]])]});
            var Q3;
            Q3=makeQuery(id+"F2.opExtrude","CAP_FACE",FACE,{"disambiguationData":[OSD([sQuery(id+"F0.wireOp",EDGE,"E12"),sQuery(id+"F0.wireOp",EDGE,"E13"),sQuery(id+"F0.wireOp",EDGE,"E14"),sQuery(id+"F0.wireOp",EDGE,"E15"),sQuery(id+"F0.wireOp",EDGE,"E17.filletArc"),sQuery(id+"F0.wireOp",EDGE,"E18.filletArc"),sQuery(id+"F0.wireOp",EDGE,"E19.filletArc"),sQuery(id+"F0.wireOp",EDGE,"E20.filletArc"),sQuery(id+"F0.wireOp",EDGE,"E25.0"),sQuery(id+"F0.wireOp",EDGE,"E25.1"),sQuery(id+"F0.wireOp",EDGE,"E25.2"),sQuery(id+"F0.wireOp",EDGE,"E25.3"),sQuery(id+"F0.wireOp",EDGE,"E25.4"),sQuery(id+"F0.wireOp",EDGE,"E25.5"),sQuery(id+"F0.wireOp",EDGE,"E25.6"),sQuery(id+"F0.wireOp",EDGE,"E25.7")])],"isStart":false});
            extrude(context, id + "F17", {"entities" : qUnion([Q0, Q1, Q2]), "endBound" : BoundingType.UP_TO_SURFACE, "depth" : 25 * mm, "endBoundEntityFace" : qUnion([Q3]), "offsetDistance" : 25 * mm});
        }
    });
